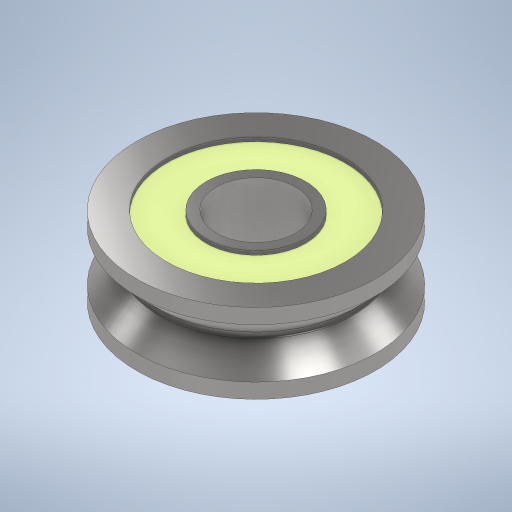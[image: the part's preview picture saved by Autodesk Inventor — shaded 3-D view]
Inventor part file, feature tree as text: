
AUTODESK INVENTOR PART (.ipt)
format: ipt  version: 2024 (Build 280153000, 153)  size: 322,048 bytes
history: native  units: mm
features: extrude x1, sketch x1, projected_geometry x1
ambient origin geometry x8: Origin, YZ Plane, XZ Plane, XY Plane, X Axis, Y Axis, Z Axis, Center Point
bodies: Solid1 (feature_tree), Body2 (feature_tree)
feature tree (3):
  extrude  "Extrusion1"  [1 undecoded]
  sketch  "Sketch1"  dims[d0=0.2mm d1=0.0mm]
  projected_geometry  "Projected Loop1"
note: 1 required parameter value undecoded (feature->parameter linkage not recoverable at this tier; creation-order binding heuristic only, values carry confidence <= 0.55)
